# Revit family: ASL_Designline_AL_Door_100mm_Jamb
name_source: partatom
category: Detail Items
revit_build: Autodesk Revit 2018 (Build: 20170223_1515(x64)
units: mm (PartAtom-declared; Revit-internal decimal feet)

## family parameters
Rotate with component = No
Section Shape = Not Defined
Shared = Yes

## types (2) — shared parameters
64mm Steel Stud = No
92mm Steel Stud = No
Manufacturer = Aluminate Solutions Limited
Masking Region = Yes
Plasterboard Head Parametric = 7 mm  [stored 0.0229659 ft]
Technical Info = www.aluminate.nz
Timber Frame = Yes

## per-type parameters (varying)
| type | 10mm Plasterboard | 13mm Plasterboard | 50mm Door Jamb Standard | ASL 415 | ASL 420 | ASL Hinge Stile Hinge Door 100mm | Glazing | Hinge_Single | Masking Region Parametric | Type Comments |
| ASL 415 Timber Frame Wall Glazing | Yes | No | No | Yes | No | No | Yes | No | 62 mm | ASL Designline ASL 415 Jamb With 90mm Timber Stud With Glazing |
| ASL 415 Timber Frame Wall Single Action ASL Hinge Stile Door Suite 100mm | No | Yes | Yes | No | Yes | Yes | No | Yes | 66 mm  [stored 0.216535 ft] | ASL Designline ASL 415 Jamb With 90mm Timber Stud With ASL 100mm Hinge Stile Door Suite |

note: [stored X ft] marks values corroborated as IEEE doubles in the binary element streams (Revit-internal decimal feet)

## geometry (parser evidence)
native form markers: Sweep x12
no freeform markers — native parametric forms only
